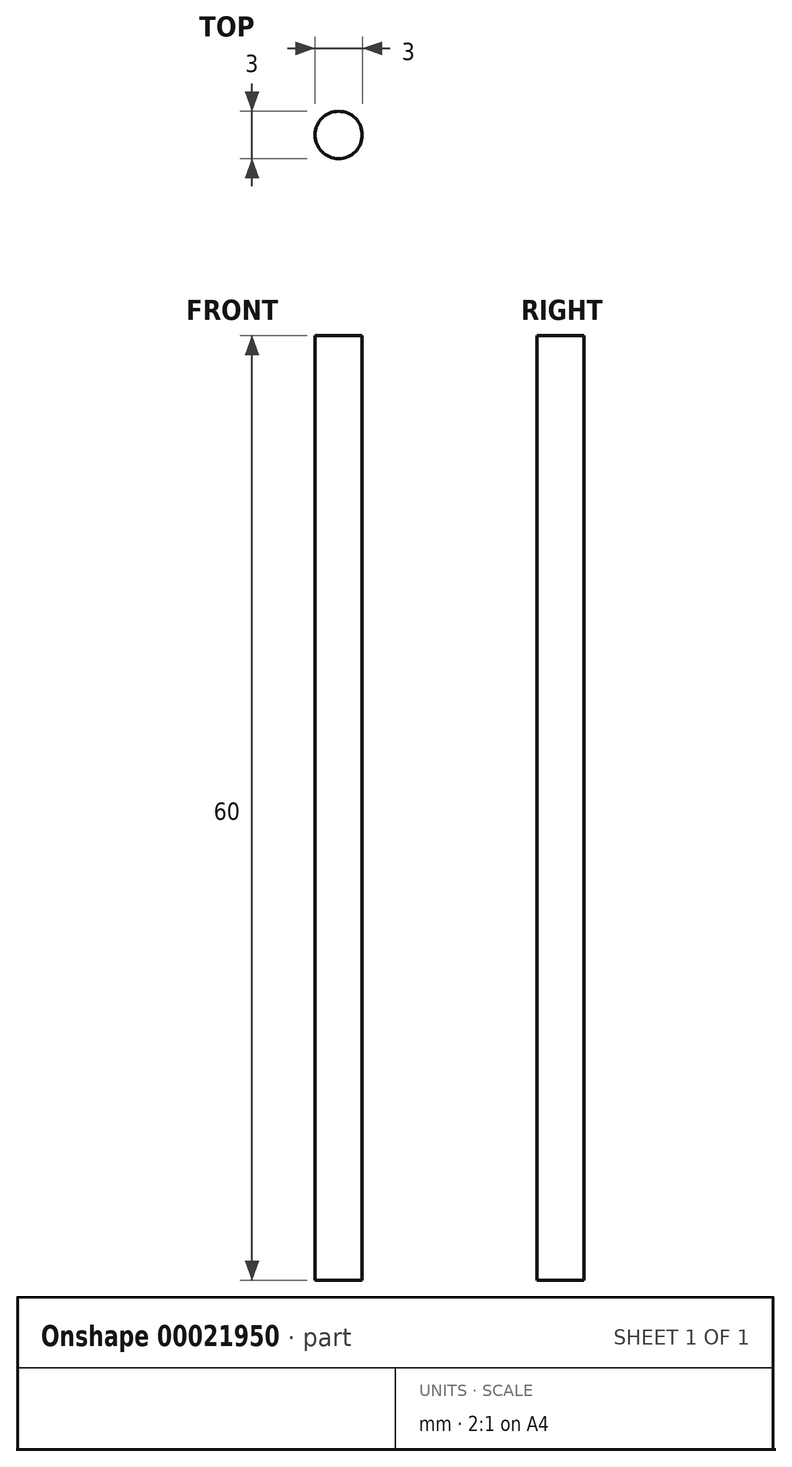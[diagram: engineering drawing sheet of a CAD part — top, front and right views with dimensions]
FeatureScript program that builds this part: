
annotation { "Feature Type Name" : "Feature", "Feature Type Description" : "" }
export const myFeature = defineFeature(function(context is Context, id is Id, definition is map)
    precondition{}
    {
        {
            var Q0;
            Q0=qCreatedBy(makeId("Top.planeOp"),FACE);
            var sketch = newSketch(context, id + "F0", { "sketchPlane" : qUnion([Q0])});
            skCircle(sketch, "E0", {"center": v(-11.02, -2.27) * mm, "radius": 1.5 * mm});
            skSolve(sketch);
        }
        {
            var Q0;
            Q0=makeQuery(id+"F0.imprint","IMPRINT",FACE,{"disambiguationData":[TD([[makeQuery(id+"F0.imprint","IMPRINT",EDGE,{"derivedFrom":sQuery(id+"F0.wireOp",EDGE,"E0")}),1.0]])]});
            extrude(context, id + "F1", {"entities" : qUnion([Q0]), "depth" : 60 * mm});
        }
    });
